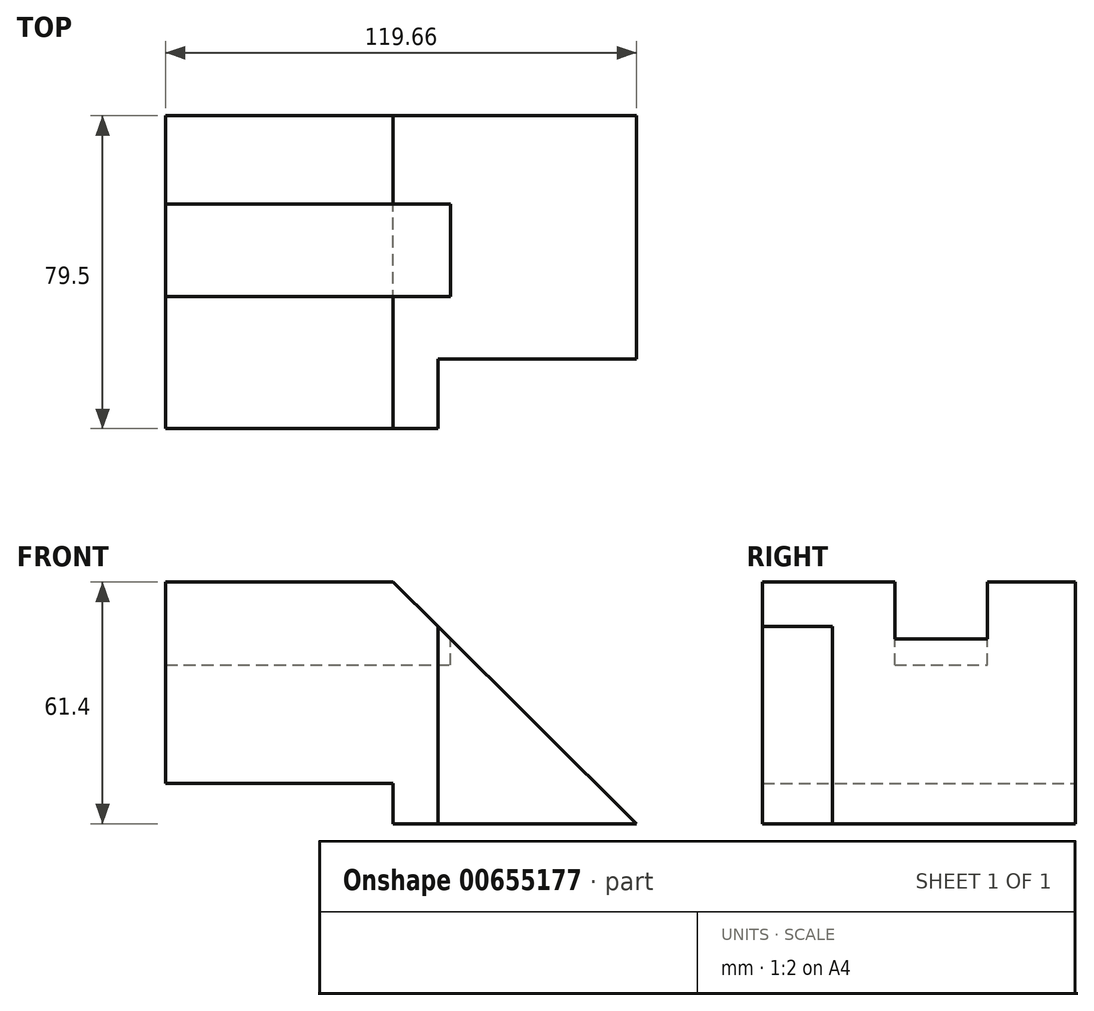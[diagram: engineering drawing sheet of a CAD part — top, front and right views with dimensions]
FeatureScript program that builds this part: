
annotation { "Feature Type Name" : "Feature", "Feature Type Description" : "" }
export const myFeature = defineFeature(function(context is Context, id is Id, definition is map)
    precondition{}
    {
        {
            var Q0;
            Q0=qCreatedBy(makeId("Front.planeOp"),FACE);
            var sketch = newSketch(context, id + "F0", { "sketchPlane" : qUnion([Q0])});
            skLineSegment(sketch, "E0", {"start": v(-57.83, 37.55) * mm, "end": v(-57.83, -13.56) * mm});
            skLineSegment(sketch, "E1", {"start": v(-57.83, -13.56) * mm, "end": v(0, -13.56) * mm});
            skLineSegment(sketch, "E2", {"start": v(0, -13.56) * mm, "end": v(0, -23.85) * mm});
            skLineSegment(sketch, "E3", {"start": v(0, -23.85) * mm, "end": v(61.83, -23.85) * mm});
            skLineSegment(sketch, "E4", {"start": v(61.83, -23.85) * mm, "end": v(0, 37.55) * mm});
            skLineSegment(sketch, "E5", {"start": v(0, 37.55) * mm, "end": v(-57.83, 37.55) * mm});
            skSolve(sketch);
        }
        {
            var Q0;
            Q0=makeQuery(id+"F0.imprint","IMPRINT",FACE,{"disambiguationData":[TD([[makeQuery(id+"F0.imprint","IMPRINT",EDGE,{"derivedFrom":sQuery(id+"F0.wireOp",EDGE,"E0")}),1.0]])]});
            extrude(context, id + "F1", {"entities" : qUnion([Q0]), "depth" : 79.5 * mm, "offsetDistance" : 25.4 * mm});
        }
        {
            var Q0;
            Q0=makeQuery(id+"F1.opExtrude","SWEPT_FACE",FACE,{"disambiguationData":[OSD([sQuery(id+"F0.wireOp",EDGE,"E5")])]});
            var sketch = newSketch(context, id + "F2", { "sketchPlane" : qUnion([Q0])});
            skLineSegment(sketch, "E6.bottom", {"start": v(-88.72, -16.57) * mm, "end": v(21.17, -16.57) * mm});
            skLineSegment(sketch, "E6.top", {"start": v(-88.72, -54.1) * mm, "end": v(21.17, -54.1) * mm});
            skLineSegment(sketch, "E6.left", {"start": v(-88.72, -16.57) * mm, "end": v(-88.72, -54.1) * mm});
            skLineSegment(sketch, "E6.right", {"start": v(21.17, -16.57) * mm, "end": v(21.17, -54.1) * mm});
            skPoint(sketch, "E6.middle", {"position": v(-33.77, -35.34) * mm});
            skSolve(sketch);
        }
        {
            var Q0;
            {var subQ0=sQuery(id+"F2.wireOp",EDGE,"E6.left");Q0=makeQuery(id+"F2.imprint","IMPRINT",FACE,{"disambiguationData":[TD([[makeQuery(id+"F2.imprint","IMPRINT",EDGE,{"derivedFrom":subQ0}),1.0]])]});}
            extrude(context, id + "F3", {"entities" : qUnion([Q0]), "operationType" : NewBodyOperationType.REMOVE, "oppositeDirection" : true, "depth" : 25.4 * mm, "offsetDistance" : 25.4 * mm});
        }
        {
            var Q0;
            Q0=makeQuery(id+"F1.opExtrude","SWEPT_FACE",FACE,{"disambiguationData":[OSD([sQuery(id+"F0.wireOp",EDGE,"E5")])]});
            var sketch = newSketch(context, id + "F4", { "sketchPlane" : qUnion([Q0])});
            skLineSegment(sketch, "E7.bottom", {"start": v(-57.83, -49.43) * mm, "end": v(0, -49.43) * mm});
            skLineSegment(sketch, "E7.top", {"start": v(-57.83, -25.27) * mm, "end": v(0, -25.27) * mm});
            skLineSegment(sketch, "E7.left", {"start": v(-57.83, -49.43) * mm, "end": v(-57.83, -25.27) * mm});
            skLineSegment(sketch, "E7.right", {"start": v(0, -49.43) * mm, "end": v(0, -25.27) * mm});
            skSolve(sketch);
        }
        {
            var Q0;
            Q0=makeQuery(id+"F4.imprint","IMPRINT",FACE,{"disambiguationData":[TD([[makeQuery(id+"F4.imprint","IMPRINT",EDGE,{"derivedFrom":sQuery(id+"F4.wireOp",EDGE,"E7.bottom")}),1.0]])]});
            extrude(context, id + "F5", {"entities" : qUnion([Q0]), "operationType" : NewBodyOperationType.ADD, "oppositeDirection" : true, "depth" : 12.45 * mm, "offsetDistance" : 25.4 * mm});
        }
        {
            var Q0;
            Q0=makeQuery(id+"F1.opExtrude","SWEPT_FACE",FACE,{"disambiguationData":[OSD([sQuery(id+"F0.wireOp",EDGE,"E5")])]});
            var sketch = newSketch(context, id + "F6", { "sketchPlane" : qUnion([Q0])});
            skLineSegment(sketch, "E8.bottom", {"start": v(-57.83, -45.88) * mm, "end": v(14.56, -45.88) * mm});
            skLineSegment(sketch, "E8.top", {"start": v(-57.83, -22.39) * mm, "end": v(14.56, -22.39) * mm});
            skLineSegment(sketch, "E8.left", {"start": v(-57.83, -45.88) * mm, "end": v(-57.83, -22.39) * mm});
            skLineSegment(sketch, "E8.right", {"start": v(14.56, -45.88) * mm, "end": v(14.56, -22.39) * mm});
            skSolve(sketch);
        }
        {
            var Q0;
            Q0 = qSketchRegion(id + "F6", true);
            extrude(context, id + "F7", {"entities" : qUnion([Q0]), "operationType" : NewBodyOperationType.REMOVE, "oppositeDirection" : true, "depth" : 21.08 * mm, "offsetDistance" : 25.4 * mm});
        }
        {
            var Q0;
            Q0=makeQuery(id+"F1.opExtrude","SWEPT_FACE",FACE,{"disambiguationData":[OSD([sQuery(id+"F0.wireOp",EDGE,"E3")])]});
            var sketch = newSketch(context, id + "F8", { "sketchPlane" : qUnion([Q0])});
            skLineSegment(sketch, "E9.bottom", {"start": v(11.33, 79.5) * mm, "end": v(61.83, 79.5) * mm});
            skLineSegment(sketch, "E9.top", {"start": v(11.33, 61.76) * mm, "end": v(61.83, 61.76) * mm});
            skLineSegment(sketch, "E9.left", {"start": v(11.33, 79.5) * mm, "end": v(11.33, 61.76) * mm});
            skLineSegment(sketch, "E9.right", {"start": v(61.83, 79.5) * mm, "end": v(61.83, 61.76) * mm});
            skSolve(sketch);
        }
        {
            var Q0;
            Q0=makeQuery(id+"F8.imprint","IMPRINT",FACE,{"disambiguationData":[TD([[makeQuery(id+"F8.imprint","IMPRINT",EDGE,{"derivedFrom":sQuery(id+"F8.wireOp",EDGE,"E9.bottom")}),-1.0]])]});
            extrude(context, id + "F9", {"entities" : qUnion([Q0]), "operationType" : NewBodyOperationType.REMOVE, "oppositeDirection" : true, "depth" : 56.4 * mm, "offsetDistance" : 25.4 * mm});
        }
        {
            var Q0;
            Q0=makeQuery(id+"F1.opExtrude","SWEPT_FACE",FACE,{"disambiguationData":[OSD([sQuery(id+"F0.wireOp",EDGE,"E4")])]});
            var sketch = newSketch(context, id + "F10", { "sketchPlane" : qUnion([Q0])});
            skCircle(sketch, "E10", {"center": v(11.48, -48.85) * mm, "radius": 8.23 * mm});
            skCircle(sketch, "E11", {"center": v(46.08, -50.13) * mm, "radius": 9.37 * mm});
            skCircle(sketch, "E12", {"center": v(10.18, -14.76) * mm, "radius": 8.12 * mm});
            skCircle(sketch, "E13", {"center": v(44.26, -14.02) * mm, "radius": 9.34 * mm});
            skSolve(sketch);
        }
        {
            var Q0;
            Q0 = qSketchRegion(id + "F10", true);
            extrude(context, id + "F11", {"entities" : qUnion([Q0]), "operationType" : NewBodyOperationType.REMOVE, "oppositeDirection" : true, "depth" : 85.34 * mm, "offsetDistance" : 25.4 * mm});
        }
    });
